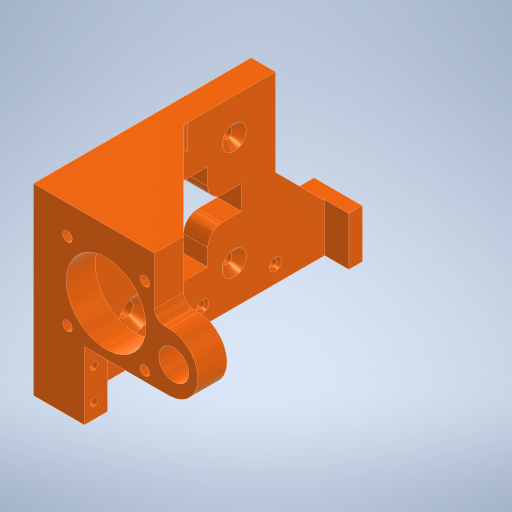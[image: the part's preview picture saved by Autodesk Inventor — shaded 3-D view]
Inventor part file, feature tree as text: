
AUTODESK INVENTOR PART (.ipt)
format: ipt  version: 2024.1 (Build 281209000, 209)  size: 475,648 bytes
history: native  units: in
note: dims shown in document units (in); Inventor stores cm internally (conversion verified against a paired STEP export)
features: extrude x18, sketch x18, chamfer x5, fillet x4
ambient origin geometry x8: Origin, YZ Plane, XZ Plane, XY Plane, X Axis, Y Axis, Z Axis, Center Point
bodies: Solid1 (feature_tree)
feature tree (45):
  extrude  "Extrusion1"  Depth=1.4961in
  extrude  "Extrusion2"  Depth=0.9449in
  extrude  "Extrusion3"  Depth=0.7874in TaperAngle=0.0deg
  extrude  "Extrusion4"  Depth=0.3937in
  extrude  "Extrusion5"  Depth=0.0787in
  fillet  "Fillet1"  Radius=0.0787in
  extrude  "Extrusion6"  Depth=0.0787in
  extrude  "Extrusion7"  Depth=0.315in
  chamfer  "Chamfer1"  [1 undecoded]
  chamfer  "Chamfer2"  Distance=0.7874in
  extrude  "Extrusion8"  Depth=0.0787in
  chamfer  "Chamfer3"  [1 undecoded]
  extrude  "Extrusion9"  Depth=0.1181in
  chamfer  "Chamfer4"  Distance=0.1181in
  extrude  "Extrusion10"  Depth=0.1575in
  extrude  "Extrusion15"  Depth=0.0787in
  extrude  "Extrusion16"  Depth=0.0787in
  extrude  "Extrusion17"  Depth=0.1575in
  extrude  "Extrusion18"  TaperAngle=0.0deg  [1 undecoded]
  extrude  "Extrusion19"  Depth=0.0591in TaperAngle=45.0deg
  chamfer  "Chamfer5"  Distance=0.0787in Angle=45.0deg
  extrude  "Extrusion20"  Depth=1.1024in
  extrude  "Extrusion21"  Depth=0.3937in
  fillet  "Fillet3"  [1 undecoded]
  extrude  "Extrusion22"  Depth=0.3937in TaperAngle=45.0deg
  fillet  "Fillet5"  Radius=0.0787in
  fillet  "Fillet6"  Radius=0.0787in
  sketch  "Sketch1"  dims[d0=1.4961in d1=2.1654in]
  sketch  "Sketch2"  dims[d2=0.1969in d3=0.0in d4=0.9449in]
  sketch  "Sketch3"  dims[d5=0.2362in d6=0.7874in d7=0.0in]
  sketch  "Sketch4"  dims[d8=0.6496in d9=0.3937in]
  sketch  "Sketch5"  dims[d10=0.3937in d11=0.0787in d12=0.0787in]
  sketch  "Sketch6"  dims[d13=0.0787in d14=0.0787in]
  sketch  "Sketch7"  dims[d15=0.315in d16=0.315in]
  sketch  "Sketch8"  dims[d17=0.315in]
  sketch  "Sketch9"  dims[d18=0.315in]
  sketch  "Sketch10"  dims[d19=0.315in]
  sketch  "Sketch15"  dims[d20=0.315in]
  sketch  "Sketch16"  dims[d21=0.315in]
  sketch  "Sketch17"  dims[d22=0.315in d23=0.0in d24=0.0in]
  sketch  "Sketch18"  dims[d25=0.1181in d26=0.7874in d27=0.0in]
  sketch  "Sketch19"  dims[d28=0.0in d29=0.0in d30=0.0787in]
  sketch  "Sketch20"  dims[d31=0.0787in]
  sketch  "Sketch21"  dims[d32=0.7087in]
  sketch  "Sketch22"  dims[d33=1.378in d34=0.0in d35=0.0in d36=0.1181in d37=0.1181in d38=0.1575in d39=0.4331in d40=0.4331in d41=0.1575in d42=0.0in d43=0.0in d44=0.0591in d45=0.0787in d46=45.0deg d47=0.0748in d48=0.0787in d49=45.0deg d50=1.1024in d51=0.3937in d52=0.0in d53=0.0in d54=0.3937in d55=0.0787in d56=45.0deg d57=0.0787in d58=0.0787in d59=0.2953in d60=0.7283in d61=0.315in d62=0.7283in d63=0.0in d64=0.0in d65=0.0591in d66=0.0787in d67=45.0deg d68=0.0591in d69=0.0591in d70=0.0591in d71=0.1378in d72=0.3937in d73=0.1378in d74=0.5906in d76=0.1378in d77=0.0in d78=0.0in d95=0.5906in d96=0.1181in d97=0.3937in d98=0.2165in d99=0.0in d100=0.1102in d101=0.1969in d102=0.0in d103=0.189in d104=0.2165in d105=0.0in d106=0.0591in d107=0.0591in d108=0.2559in d109=0.1181in d110=0.0787in d111=0.0787in d112=0.0in d113=0.0in d114=0.1969in d115=0.3937in d116=0.3937in d117=0.5512in d118=0.0in d119=0.0in d120=0.0197in d121=0.0787in d122=45.0deg d123=0.4724in d124=0.3543in d125=0.0in d126=0.2441in d127=0.2362in d128=0.1969in d129=0.0in d130=0.0in d132=0.2362in d134=0.1969in d135=0.2559in d136=0.2756in d137=0.0in d138=0.0in d139=0.1181in d152=0.0787in]
note: 4 required parameter values undecoded (feature->parameter linkage not recoverable at this tier; creation-order binding heuristic only, values carry confidence <= 0.55)
